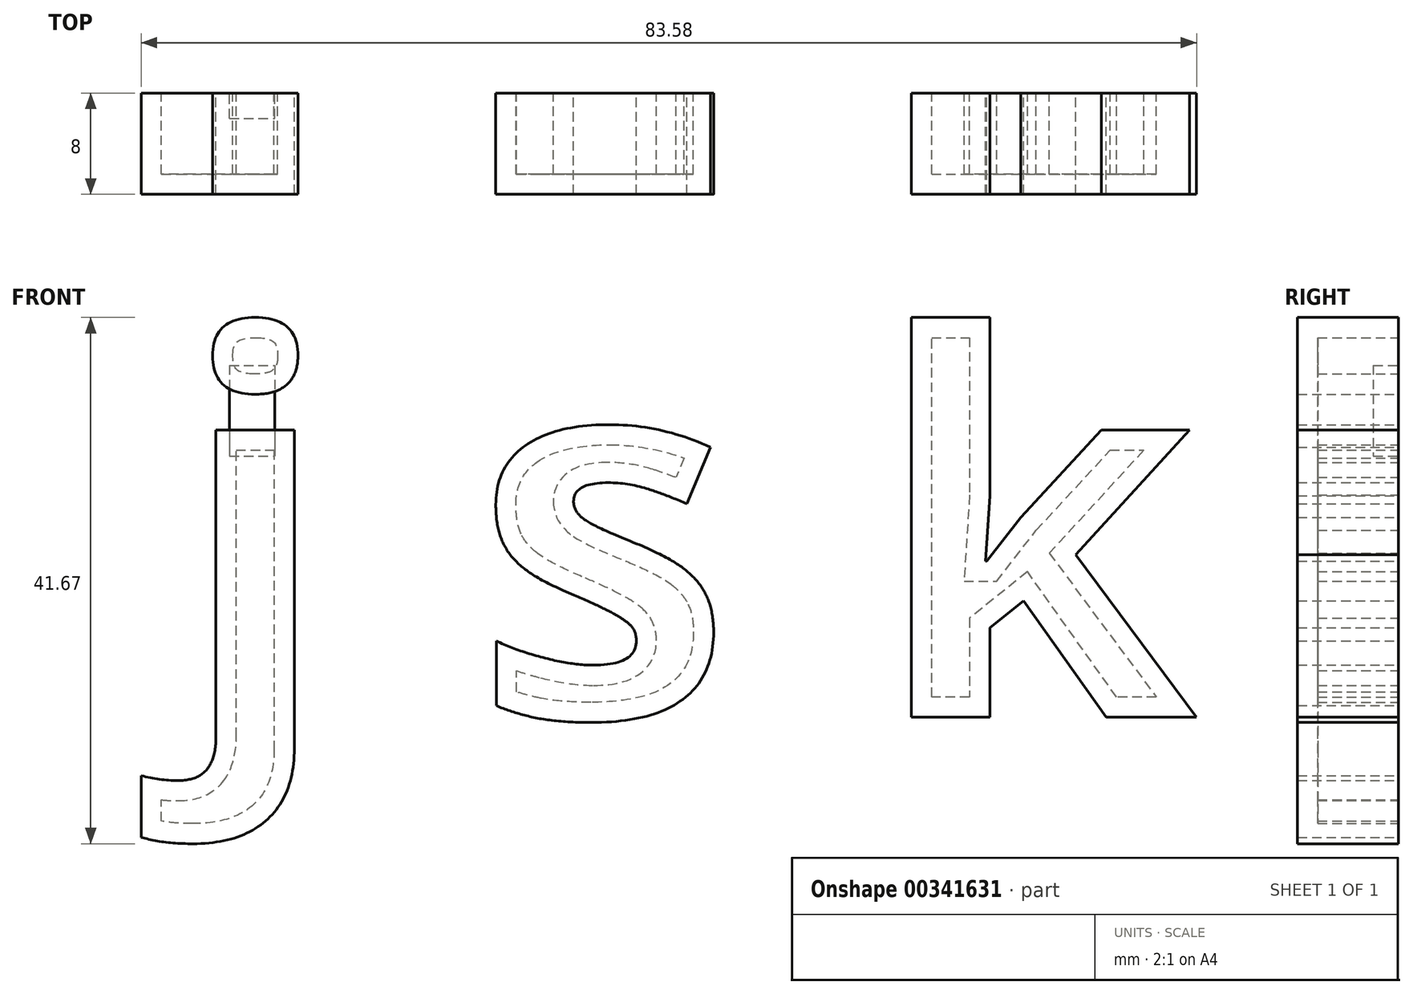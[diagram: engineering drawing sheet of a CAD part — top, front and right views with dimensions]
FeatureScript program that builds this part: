
annotation { "Feature Type Name" : "Feature", "Feature Type Description" : "" }
export const myFeature = defineFeature(function(context is Context, id is Id, definition is map)
    precondition{}
    {
        {
            var Q0;
            Q0=qCreatedBy(makeId("Front.planeOp"),FACE);
            var sketch = newSketch(context, id + "F0", { "sketchPlane" : qUnion([Q0])});
            skPoint(sketch, "E0.firstSnap0", {"position": v(-14.3, 26.8) * mm});
            skText(sketch, "E1", { "text": "j s k\n", "fontName": "OpenSans-Bold.ttf"});
            const initialGuessF0  = {"E1": [-0.0486, -0.0429, 1, 0, 0.03]};
            skSetInitialGuess(sketch, initialGuessF0);
            skSolve(sketch);
        }
        {
            var Q0;
            Q0 = qSketchRegion(id + "F0", true);
            extrude(context, id + "F1", {"entities" : qUnion([Q0]), "depth" : 8 * mm});
        }
        {
            var Q0;
            Q0=makeQuery(id+"F1.opExtrude","CAP_FACE",FACE,{"disambiguationData":[OSD([sQuery(id+"F0.wireOp",EDGE,"E1.sketch_text.stroke-41"),sQuery(id+"F0.wireOp",EDGE,"E1.sketch_text.stroke-42"),sQuery(id+"F0.wireOp",EDGE,"E1.sketch_text.stroke-43"),sQuery(id+"F0.wireOp",EDGE,"E1.sketch_text.stroke-44"),sQuery(id+"F0.wireOp",EDGE,"E1.sketch_text.stroke-45"),sQuery(id+"F0.wireOp",EDGE,"E1.sketch_text.stroke-46"),sQuery(id+"F0.wireOp",EDGE,"E1.sketch_text.stroke-47"),sQuery(id+"F0.wireOp",EDGE,"E1.sketch_text.stroke-48"),sQuery(id+"F0.wireOp",EDGE,"E1.sketch_text.stroke-49"),sQuery(id+"F0.wireOp",EDGE,"E1.sketch_text.stroke-50"),sQuery(id+"F0.wireOp",EDGE,"E1.sketch_text.stroke-51"),sQuery(id+"F0.wireOp",EDGE,"E1.sketch_text.stroke-52"),sQuery(id+"F0.wireOp",EDGE,"E1.sketch_text.stroke-53"),sQuery(id+"F0.wireOp",EDGE,"E1.sketch_text.stroke-54"),sQuery(id+"F0.wireOp",EDGE,"E1.sketch_text.stroke-55")])],"isStart":true});
            var Q1;
            Q1=makeQuery(id+"F1.opExtrude","CAP_FACE",FACE,{"disambiguationData":[OSD([sQuery(id+"F0.wireOp",EDGE,"E1.sketch_text.stroke-15"),sQuery(id+"F0.wireOp",EDGE,"E1.sketch_text.stroke-16"),sQuery(id+"F0.wireOp",EDGE,"E1.sketch_text.stroke-17"),sQuery(id+"F0.wireOp",EDGE,"E1.sketch_text.stroke-18"),sQuery(id+"F0.wireOp",EDGE,"E1.sketch_text.stroke-19"),sQuery(id+"F0.wireOp",EDGE,"E1.sketch_text.stroke-20"),sQuery(id+"F0.wireOp",EDGE,"E1.sketch_text.stroke-21"),sQuery(id+"F0.wireOp",EDGE,"E1.sketch_text.stroke-22"),sQuery(id+"F0.wireOp",EDGE,"E1.sketch_text.stroke-23"),sQuery(id+"F0.wireOp",EDGE,"E1.sketch_text.stroke-24"),sQuery(id+"F0.wireOp",EDGE,"E1.sketch_text.stroke-25"),sQuery(id+"F0.wireOp",EDGE,"E1.sketch_text.stroke-26"),sQuery(id+"F0.wireOp",EDGE,"E1.sketch_text.stroke-27"),sQuery(id+"F0.wireOp",EDGE,"E1.sketch_text.stroke-28"),sQuery(id+"F0.wireOp",EDGE,"E1.sketch_text.stroke-29"),sQuery(id+"F0.wireOp",EDGE,"E1.sketch_text.stroke-30"),sQuery(id+"F0.wireOp",EDGE,"E1.sketch_text.stroke-31"),sQuery(id+"F0.wireOp",EDGE,"E1.sketch_text.stroke-32"),sQuery(id+"F0.wireOp",EDGE,"E1.sketch_text.stroke-33"),sQuery(id+"F0.wireOp",EDGE,"E1.sketch_text.stroke-34"),sQuery(id+"F0.wireOp",EDGE,"E1.sketch_text.stroke-35"),sQuery(id+"F0.wireOp",EDGE,"E1.sketch_text.stroke-36"),sQuery(id+"F0.wireOp",EDGE,"E1.sketch_text.stroke-37"),sQuery(id+"F0.wireOp",EDGE,"E1.sketch_text.stroke-38"),sQuery(id+"F0.wireOp",EDGE,"E1.sketch_text.stroke-39"),sQuery(id+"F0.wireOp",EDGE,"E1.sketch_text.stroke-40")])],"isStart":true});
            var Q2;
            Q2=makeQuery(id+"F1.opExtrude","CAP_FACE",FACE,{"disambiguationData":[OSD([sQuery(id+"F0.wireOp",EDGE,"E1.sketch_text.stroke-0"),sQuery(id+"F0.wireOp",EDGE,"E1.sketch_text.stroke-1"),sQuery(id+"F0.wireOp",EDGE,"E1.sketch_text.stroke-2"),sQuery(id+"F0.wireOp",EDGE,"E1.sketch_text.stroke-3"),sQuery(id+"F0.wireOp",EDGE,"E1.sketch_text.stroke-4"),sQuery(id+"F0.wireOp",EDGE,"E1.sketch_text.stroke-5"),sQuery(id+"F0.wireOp",EDGE,"E1.sketch_text.stroke-6"),sQuery(id+"F0.wireOp",EDGE,"E1.sketch_text.stroke-7"),sQuery(id+"F0.wireOp",EDGE,"E1.sketch_text.stroke-8"),sQuery(id+"F0.wireOp",EDGE,"E1.sketch_text.stroke-9")])],"isStart":true});
            var Q3;
            Q3=makeQuery(id+"F1.opExtrude","CAP_FACE",FACE,{"disambiguationData":[OSD([sQuery(id+"F0.wireOp",EDGE,"E1.sketch_text.stroke-10"),sQuery(id+"F0.wireOp",EDGE,"E1.sketch_text.stroke-11"),sQuery(id+"F0.wireOp",EDGE,"E1.sketch_text.stroke-12"),sQuery(id+"F0.wireOp",EDGE,"E1.sketch_text.stroke-13"),sQuery(id+"F0.wireOp",EDGE,"E1.sketch_text.stroke-14")])],"isStart":true});
            var Q4;
            Q4=makeQuery(id+"F1.opExtrude","SWEPT_BODY",BODY,{"disambiguationData":[OSD([sQuery(id+"F0.wireOp",EDGE,"E1.sketch_text.stroke-41"),sQuery(id+"F0.wireOp",EDGE,"E1.sketch_text.stroke-42"),sQuery(id+"F0.wireOp",EDGE,"E1.sketch_text.stroke-43"),sQuery(id+"F0.wireOp",EDGE,"E1.sketch_text.stroke-44"),sQuery(id+"F0.wireOp",EDGE,"E1.sketch_text.stroke-45"),sQuery(id+"F0.wireOp",EDGE,"E1.sketch_text.stroke-46"),sQuery(id+"F0.wireOp",EDGE,"E1.sketch_text.stroke-47"),sQuery(id+"F0.wireOp",EDGE,"E1.sketch_text.stroke-48"),sQuery(id+"F0.wireOp",EDGE,"E1.sketch_text.stroke-49"),sQuery(id+"F0.wireOp",EDGE,"E1.sketch_text.stroke-50"),sQuery(id+"F0.wireOp",EDGE,"E1.sketch_text.stroke-51"),sQuery(id+"F0.wireOp",EDGE,"E1.sketch_text.stroke-52"),sQuery(id+"F0.wireOp",EDGE,"E1.sketch_text.stroke-53"),sQuery(id+"F0.wireOp",EDGE,"E1.sketch_text.stroke-54"),sQuery(id+"F0.wireOp",EDGE,"E1.sketch_text.stroke-55")])]});
            var Q5;
            Q5=makeQuery(id+"F1.opExtrude","SWEPT_BODY",BODY,{"disambiguationData":[OSD([sQuery(id+"F0.wireOp",EDGE,"E1.sketch_text.stroke-15"),sQuery(id+"F0.wireOp",EDGE,"E1.sketch_text.stroke-16"),sQuery(id+"F0.wireOp",EDGE,"E1.sketch_text.stroke-17"),sQuery(id+"F0.wireOp",EDGE,"E1.sketch_text.stroke-18"),sQuery(id+"F0.wireOp",EDGE,"E1.sketch_text.stroke-19"),sQuery(id+"F0.wireOp",EDGE,"E1.sketch_text.stroke-20"),sQuery(id+"F0.wireOp",EDGE,"E1.sketch_text.stroke-21"),sQuery(id+"F0.wireOp",EDGE,"E1.sketch_text.stroke-22"),sQuery(id+"F0.wireOp",EDGE,"E1.sketch_text.stroke-23"),sQuery(id+"F0.wireOp",EDGE,"E1.sketch_text.stroke-24"),sQuery(id+"F0.wireOp",EDGE,"E1.sketch_text.stroke-25"),sQuery(id+"F0.wireOp",EDGE,"E1.sketch_text.stroke-26"),sQuery(id+"F0.wireOp",EDGE,"E1.sketch_text.stroke-27"),sQuery(id+"F0.wireOp",EDGE,"E1.sketch_text.stroke-28"),sQuery(id+"F0.wireOp",EDGE,"E1.sketch_text.stroke-29"),sQuery(id+"F0.wireOp",EDGE,"E1.sketch_text.stroke-30"),sQuery(id+"F0.wireOp",EDGE,"E1.sketch_text.stroke-31"),sQuery(id+"F0.wireOp",EDGE,"E1.sketch_text.stroke-32"),sQuery(id+"F0.wireOp",EDGE,"E1.sketch_text.stroke-33"),sQuery(id+"F0.wireOp",EDGE,"E1.sketch_text.stroke-34"),sQuery(id+"F0.wireOp",EDGE,"E1.sketch_text.stroke-35"),sQuery(id+"F0.wireOp",EDGE,"E1.sketch_text.stroke-36"),sQuery(id+"F0.wireOp",EDGE,"E1.sketch_text.stroke-37"),sQuery(id+"F0.wireOp",EDGE,"E1.sketch_text.stroke-38"),sQuery(id+"F0.wireOp",EDGE,"E1.sketch_text.stroke-39"),sQuery(id+"F0.wireOp",EDGE,"E1.sketch_text.stroke-40")])]});
            var Q6;
            Q6=makeQuery(id+"F1.opExtrude","SWEPT_BODY",BODY,{"disambiguationData":[OSD([sQuery(id+"F0.wireOp",EDGE,"E1.sketch_text.stroke-0"),sQuery(id+"F0.wireOp",EDGE,"E1.sketch_text.stroke-1"),sQuery(id+"F0.wireOp",EDGE,"E1.sketch_text.stroke-2"),sQuery(id+"F0.wireOp",EDGE,"E1.sketch_text.stroke-3"),sQuery(id+"F0.wireOp",EDGE,"E1.sketch_text.stroke-4"),sQuery(id+"F0.wireOp",EDGE,"E1.sketch_text.stroke-5"),sQuery(id+"F0.wireOp",EDGE,"E1.sketch_text.stroke-6"),sQuery(id+"F0.wireOp",EDGE,"E1.sketch_text.stroke-7"),sQuery(id+"F0.wireOp",EDGE,"E1.sketch_text.stroke-8"),sQuery(id+"F0.wireOp",EDGE,"E1.sketch_text.stroke-9")])]});
            var Q7;
            Q7=makeQuery(id+"F1.opExtrude","SWEPT_BODY",BODY,{"disambiguationData":[OSD([sQuery(id+"F0.wireOp",EDGE,"E1.sketch_text.stroke-10"),sQuery(id+"F0.wireOp",EDGE,"E1.sketch_text.stroke-11"),sQuery(id+"F0.wireOp",EDGE,"E1.sketch_text.stroke-12"),sQuery(id+"F0.wireOp",EDGE,"E1.sketch_text.stroke-13"),sQuery(id+"F0.wireOp",EDGE,"E1.sketch_text.stroke-14")])]});
            shell(context, id + "F2", {"entities" : qUnion([Q0, Q1, Q2, Q3]), "parts" : qUnion([Q4, Q5, Q6, Q7]), "thickness" : 1.6 * mm});
        }
        {
            var Q0;
            Q0=qCreatedBy(makeId("Front.planeOp"),FACE);
            var sketch = newSketch(context, id + "F3", { "sketchPlane" : qUnion([Q0])});
            skLineSegment(sketch, "E2.bottom", {"start": v(-44.28, -15.03) * mm, "end": v(-40.68, -15.03) * mm});
            skLineSegment(sketch, "E2.top", {"start": v(-44.28, -22.22) * mm, "end": v(-40.68, -22.22) * mm});
            skLineSegment(sketch, "E2.left", {"start": v(-44.28, -15.03) * mm, "end": v(-44.28, -22.22) * mm});
            skLineSegment(sketch, "E2.right", {"start": v(-40.68, -15.03) * mm, "end": v(-40.68, -22.22) * mm});
            skSolve(sketch);
        }
        {
            var Q0;
            Q0=makeQuery(id+"F3.imprint","IMPRINT",FACE,{"disambiguationData":[TD([[makeQuery(id+"F3.imprint","IMPRINT",EDGE,{"derivedFrom":sQuery(id+"F3.wireOp",EDGE,"E2.bottom")}),-1.0]])]});
            extrude(context, id + "F4", {"entities" : qUnion([Q0]), "depth" : 2 * mm});
        }
    });
